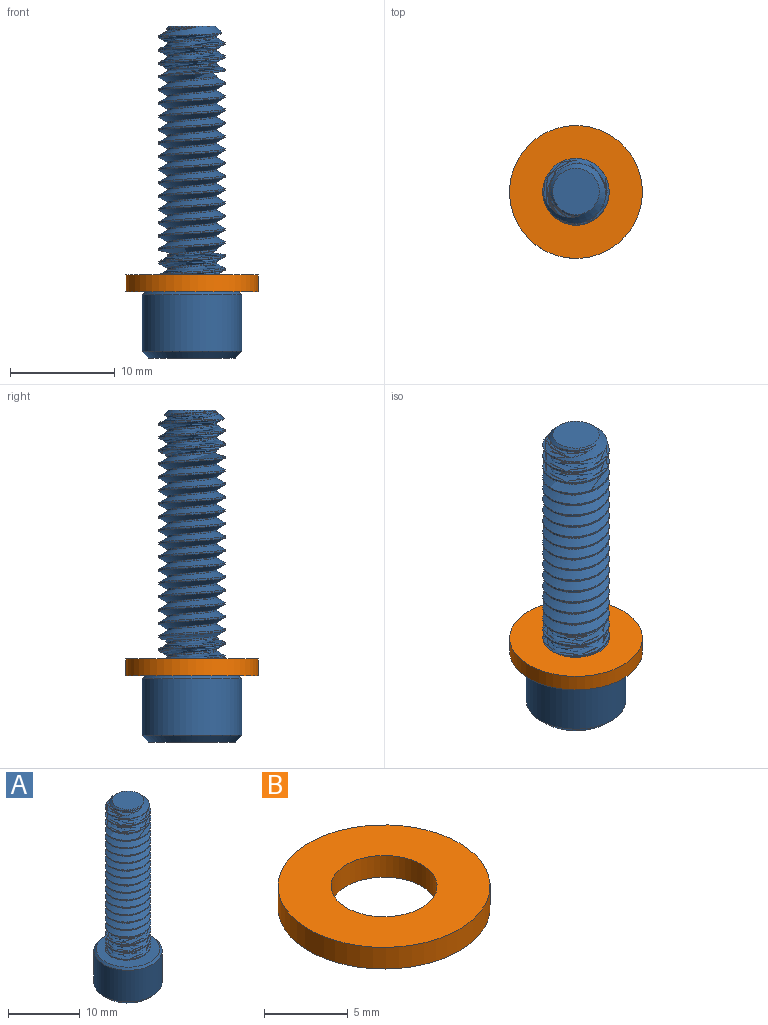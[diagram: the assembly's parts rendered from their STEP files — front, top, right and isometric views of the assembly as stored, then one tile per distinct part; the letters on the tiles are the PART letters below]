
ASSEMBLY  parts=2 mates=1
PART A: 24 faces, bbox 10.6x10.6x33.3 mm
  f0: cone r=4.76mm half-angle=45deg, axis (0,0,-1), area 13mm2, adj f3,f10
  f1: cone r=4.13mm half-angle=45deg, axis (0,0,1), area 25.1mm2, adj f3,f11
  f2: cone r=2.75mm half-angle=45deg, axis (0,0,-1), area 0.7mm2, adj f11,f22
  f3: cylinder r=4.76mm len=9.53mm, axis (0,0,1), area 161.5mm2, adj f0,f1
  f4: cylinder r=2.35mm len=25.27mm, axis (0,0,-1), area 46.6mm2, adj f5,f8,f9,f10
  f5: cone r=2.22mm half-angle=45deg, axis (0,0,-1), area 12.3mm2, adj f4,f6,f7,f8,f9
  f6: cylinder r=3.17mm len=24.45mm, axis (0,0,1), area 61mm2, adj f5,f8,f9,f10
  f7: plane 4.45x4.45mm, normal (0,0,1), area 15.5mm2, adj f5
  f8: bspline ~26.09x7.33mm, area 324mm2, adj f4,f5,f6,f10
  f9: bspline ~26.51x7.33mm, area 324.8mm2, adj f4,f5,f6,f10
  f10: plane 9.39x9.39mm, normal (0,0,1), area 37.8mm2, adj f0,f4,f6,f8,f9
  f11: plane 8.26x8.26mm, normal (0,0,-1), area 29.8mm2, adj f1,f2,f12,f13,f14,f15,f16
  f12: cone r=2.75mm half-angle=45deg, axis (0,0,-1), area 0mm2, adj f11,f18
  f13: cone r=2.75mm half-angle=45deg, axis (0,0,-1), area 0mm2, adj f11,f19
  f14: cone r=2.75mm half-angle=45deg, axis (0,0,-1), area 0mm2, adj f11,f20
  f15: cone r=2.75mm half-angle=45deg, axis (0,0,-1), area 0mm2, adj f11,f21
  f16: cone r=2.75mm half-angle=45deg, axis (0,0,-1), area 0mm2, adj f11,f23
  f17: plane 5.5x4.76mm, normal (0,0,-1), area 19.6mm2, adj f18,f19,f20,f21,f22,f23
  f18: plane 4.61x3.42mm, normal (-0.5,-0.87,0), area 9.1mm2, adj f12,f17,f19,f23
  f19: plane 4.61x3.79mm, normal (-1,0,0), area 9.2mm2, adj f13,f17,f18,f20
  f20: plane 4.61x3.42mm, normal (-0.5,0.87,0), area 9.1mm2, adj f14,f17,f19,f21
  f21: plane 4.61x3.42mm, normal (0.5,0.87,0), area 9.2mm2, adj f15,f17,f20,f22
  f22: plane 3.84x3.02mm, normal (1,0,0), area 9.2mm2, adj f2,f17,f21,f23
  f23: plane 4.61x3.42mm, normal (0.5,-0.87,0), area 9.2mm2, adj f16,f17,f18,f22
PART B: 4 faces, bbox 12.7x12.7x1.6 mm
  f0: cylinder r=3.17mm len=6.35mm, axis (0,0,-1), area 31.7mm2, adj f2,f3
  f1: cylinder r=6.35mm len=12.7mm, axis (0,0,-1), area 63.3mm2, adj f2,f3
  f2: plane 12.7x12.7mm, normal (0,0,1), area 95mm2, adj f0,f1
  f3: plane 12.7x12.7mm, normal (0,0,-1), area 95mm2, adj f0,f1
PLACE A t=(-6.61,-6.22,12.28)mm
PLACE B t=(-6.61,-6.22,9.1)mm
MATE fastened B.f0 <-> A.f0  axis (0,0,-1) through (-6.61,-6.22,-13.12)mm
